# Revit family: ME
name_source: partatom
category: Lighting Fixtures
revit_build: Autodesk Revit 2014 (Build: 20130308_1515(x64)
units: mm (PartAtom-declared; Revit-internal decimal feet)

## types (1)
- ME
    Apparent Load = 50 VA
    Assembly Code = D5020280
    Certification = The fixture is listed with ETL for outdoor, wet location use,
UL1598 and Canadian CSA Std. C22.2 no.250
    Color Filter = 16777215
    Default Elevation = 48 "
    Description = AAL's mini eSconce, now available with LED, is designed for exterior/interior environments. Available in up, down, or up + down illumination and include stainless steel and copper fascia panels. ADA compliant.
    Dimming Lamp Color Temperature Shift = <None>
    Emit Shape Visible in Rendering = No
    Emit from Rectangle Length = 4 "
    Emit from Rectangle Width = 4 "
    Finish = Hubbell-White
    Glass = Hubbell-Glass
    IP Rating = IP55
    Lamp = LED
    Load Classification = Lighting
    Manufacturer = Architectural Area Lighting
    Model = Mini-eSconce
    Photometric Web File = ME2.IES
    Photometric Web Link = https://www.hubbell.com
    Power Factor = 1
    Product Documentation Link = https://hubbellcdn.com
    Product Page URL = https://www.hubbell.com
    Tilt Angle = 0.00°
    URL = https://www.hubbell.com
    Voltage = 120 V
    Wattage Comments = 50W
    Watts = 50 W

## geometry (parser evidence)
native form markers: Blend x24, Sweep x3
no freeform markers — native parametric forms only
